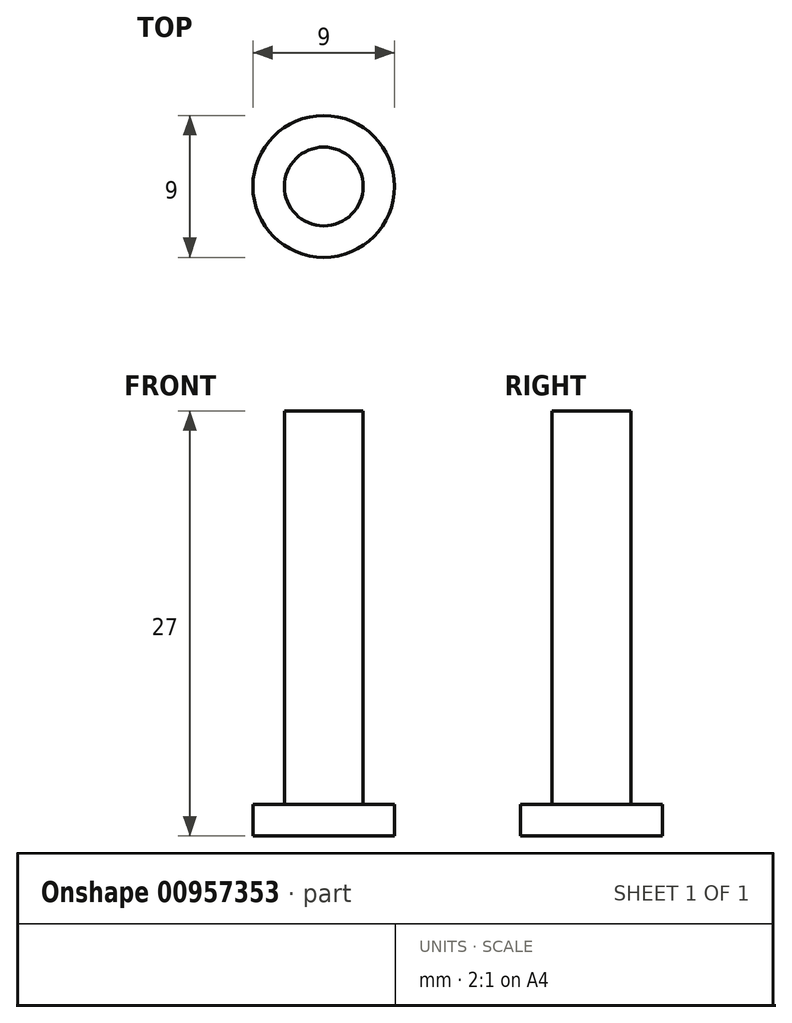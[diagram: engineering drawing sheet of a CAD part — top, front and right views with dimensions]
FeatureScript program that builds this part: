
annotation { "Feature Type Name" : "Feature", "Feature Type Description" : "" }
export const myFeature = defineFeature(function(context is Context, id is Id, definition is map)
    precondition{}
    {
        {
            var Q0;
            Q0=qCreatedBy(makeId("Front.planeOp"),FACE);
            var sketch = newSketch(context, id + "F0", { "sketchPlane" : qUnion([Q0])});
            skLineSegment(sketch, "E0", {"start": v(0, 0) * mm, "end": v(0, 27) * mm, "construction": true});
            skLineSegment(sketch, "E1", {"start": v(0, 27) * mm, "end": v(2.5, 27) * mm});
            skLineSegment(sketch, "E2", {"start": v(2.5, 27) * mm, "end": v(2.5, 2) * mm});
            skLineSegment(sketch, "E3", {"start": v(2.5, 2) * mm, "end": v(4.5, 2) * mm});
            skLineSegment(sketch, "E4", {"start": v(4.5, 2) * mm, "end": v(4.5, 0) * mm});
            skLineSegment(sketch, "E5", {"start": v(4.5, 0) * mm, "end": v(0, 0) * mm});
            skLineSegment(sketch, "E6", {"start": v(0, 27) * mm, "end": v(0, 0) * mm});
            skSolve(sketch);
        }
        {
            var Q0;
            {var subQ1=sQuery(id+"F0.wireOp",EDGE,"E2");Q0=makeQuery(id+"F0.imprint","IMPRINT",FACE,{"disambiguationData":[TD([[makeQuery(id+"F0.imprint","IMPRINT",EDGE,{"derivedFrom":subQ1}),-1.0]])]});}
            var Q1;
            Q1=sQuery(id+"F0.wireOp",EDGE,"E0");
            revolve(context, id + "F1", {"surfaceOperationType" : NewSurfaceOperationType.NEW, "entities" : qUnion([Q0]), "axis" : qUnion([Q1]), "revolveType" : RevolveType.FULL});
        }
    });
